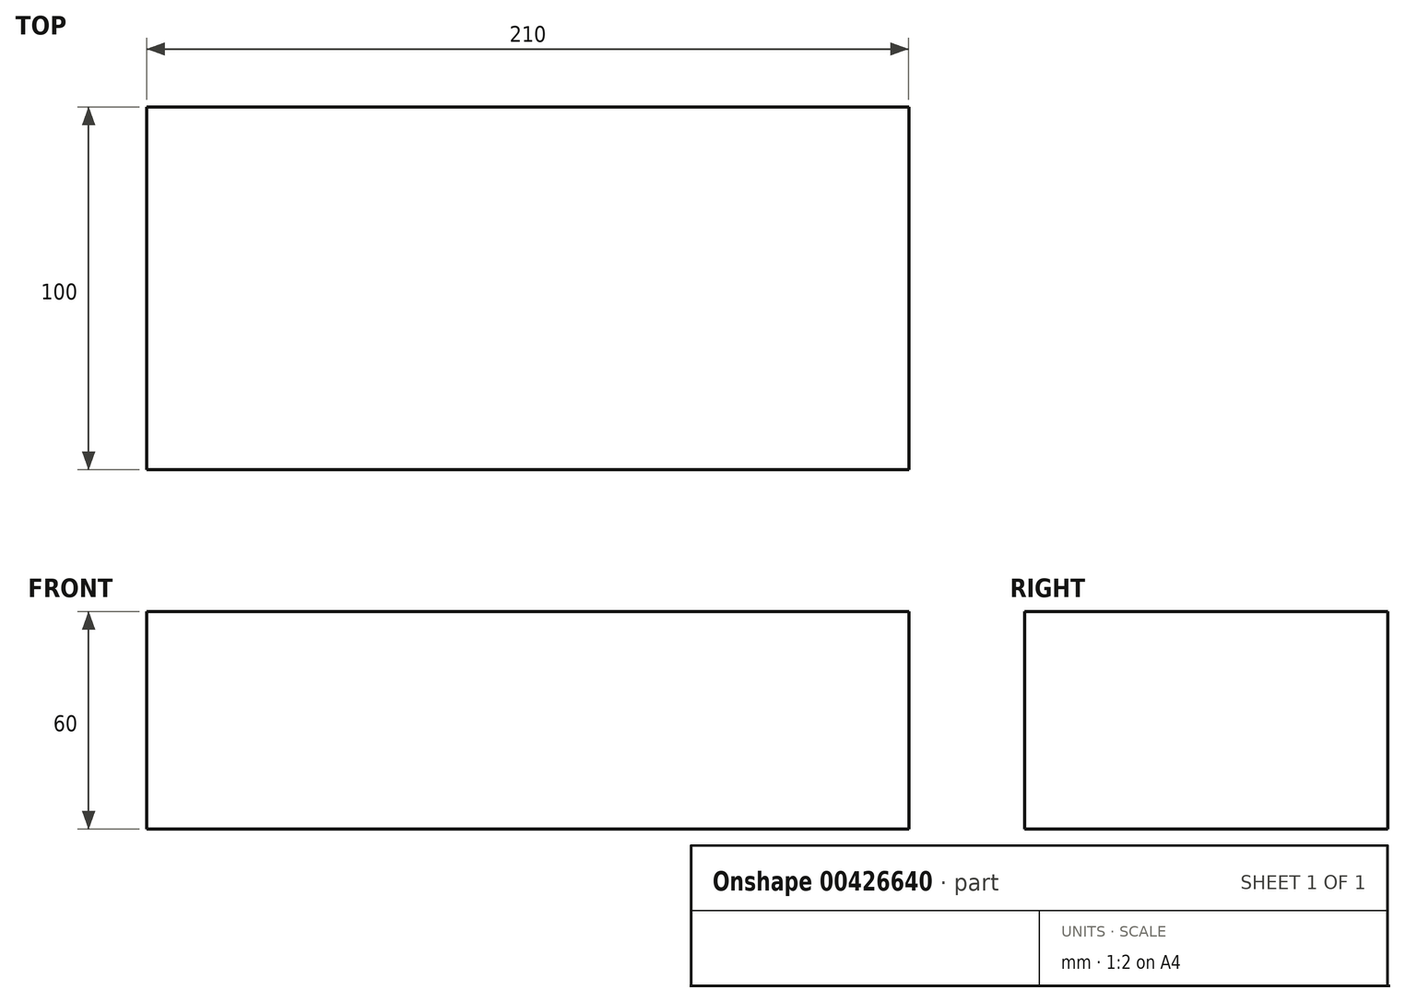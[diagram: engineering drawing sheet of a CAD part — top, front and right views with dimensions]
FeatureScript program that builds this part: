
annotation { "Feature Type Name" : "Feature", "Feature Type Description" : "" }
export const myFeature = defineFeature(function(context is Context, id is Id, definition is map)
    precondition{}
    {
        {
            var Q0;
            Q0=qCreatedBy(makeId("Top.planeOp"),FACE);
            var sketch = newSketch(context, id + "F0", { "sketchPlane" : qUnion([Q0])});
            skLineSegment(sketch, "E0.bottom", {"start": v(-118.4, 125) * mm, "end": v(91.6, 125) * mm});
            skLineSegment(sketch, "E0.top", {"start": v(-118.4, 25) * mm, "end": v(91.6, 25) * mm});
            skLineSegment(sketch, "E0.left", {"start": v(-118.4, 125) * mm, "end": v(-118.4, 25) * mm});
            skLineSegment(sketch, "E0.right", {"start": v(91.6, 125) * mm, "end": v(91.6, 25) * mm});
            skSolve(sketch);
        }
        {
            var Q0;
            Q0 = qSketchRegion(id + "F0", true);
            extrude(context, id + "F1", {"entities" : qUnion([Q0]), "depth" : 60 * mm});
        }
    });
